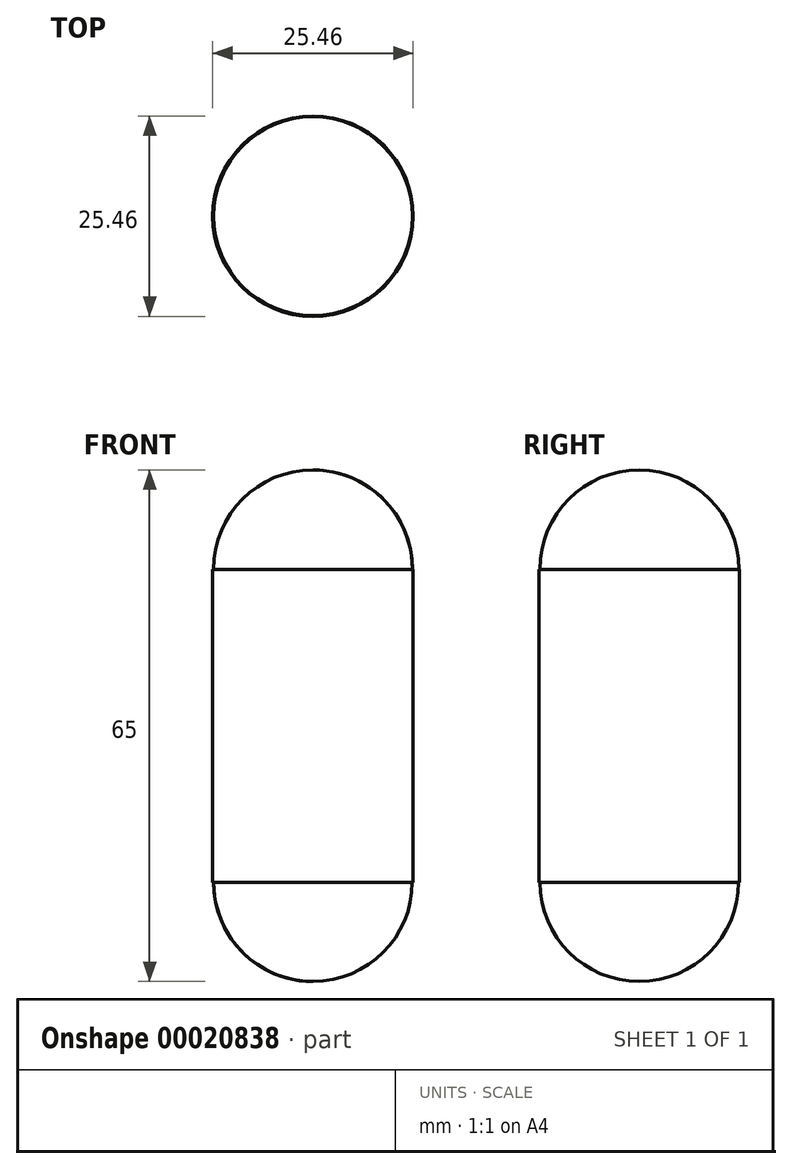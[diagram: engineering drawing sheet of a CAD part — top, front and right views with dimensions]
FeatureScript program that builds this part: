
annotation { "Feature Type Name" : "Feature", "Feature Type Description" : "" }
export const myFeature = defineFeature(function(context is Context, id is Id, definition is map)
    precondition{}
    {
        {
            var Q0;
            Q0=qCreatedBy(makeId("Front.planeOp"),FACE);
            var sketch = newSketch(context, id + "F0", { "sketchPlane" : qUnion([Q0])});
            skLineSegment(sketch, "E0.rect.bottom", {"start": v(-12.73, 19.88) * mm, "end": v(-12.63, 19.88) * mm});
            skLineSegment(sketch, "E0.rect.top", {"start": v(-12.73, -19.88) * mm, "end": v(0, -19.88) * mm});
            skLineSegment(sketch, "E0.rect.left", {"start": v(-12.73, 19.88) * mm, "end": v(-12.73, -19.88) * mm});
            skPoint(sketch, "E0.rect.middle", {"position": v(0, 0) * mm});
            skArc(sketch, "E1", {"start": v(0, 32.5) * mm, "mid": v(-12.63, 19.88) * mm, "end": v(0, 7.25) * mm});
            skArc(sketch, "E2", {"start": v(0, -7.27) * mm, "mid": v(-12.61, -19.88) * mm, "end": v(0, -32.5) * mm});
            skLineSegment(sketch, "E3", {"start": v(-12.73, 0) * mm, "end": v(0, 0) * mm});
            skLineSegment(sketch, "E4", {"start": v(0, 32.5) * mm, "end": v(0, -32.5) * mm});
            skLineSegment(sketch, "E5.trimOffspring", {"start": v(12.63, 19.88) * mm, "end": v(12.73, 19.88) * mm});
            skPoint(sketch, "E6.orphan", {"position": v(12.73, 0) * mm});
            skLineSegment(sketch, "E7.trimOffspring", {"start": v(12.61, -19.88) * mm, "end": v(12.73, -19.88) * mm});
            skSolve(sketch);
        }
        {
            var Q0;
            {var subQ4=sQuery(id+"F0.wireOp",EDGE,"E0.rect.bottom");Q0=makeQuery(id+"F0.imprint","IMPRINT",FACE,{"disambiguationData":[TD([[makeQuery(id+"F0.imprint","IMPRINT",EDGE,{"derivedFrom":subQ4}),-1.0]])]});}
            var Q1;
            {var subQ1=sQuery(id+"F0.wireOp",EDGE,"E1");var subQ4=makeQuery(id+"F0.imprint","INTERSECT",VERTEX,{"derivedFrom":[sQuery(id+"F0.wireOp",EDGE,"E0.rect.bottom"),subQ1]});Q1=makeQuery(id+"F0.imprint","IMPRINT",FACE,{"disambiguationData":[TD([[makeQuery(id+"F0.imprint","IMPRINT",EDGE,{"disambiguationData":[TD([[subQ4,1.0]])],"derivedFrom":subQ1}),1.0]])]});}
            var Q2;
            {var subQ1=sQuery(id+"F0.wireOp",EDGE,"E3");Q2=makeQuery(id+"F0.imprint","IMPRINT",FACE,{"disambiguationData":[TD([[makeQuery(id+"F0.imprint","IMPRINT",EDGE,{"derivedFrom":subQ1}),-1.0]])]});}
            var Q3;
            {var subQ0=sQuery(id+"F0.wireOp",EDGE,"E4");var subQ3=sQuery(id+"F0.wireOp",EDGE,"E0.rect.top");var subQ4=makeQuery(id+"F0.imprint","INTERSECT",VERTEX,{"derivedFrom":[subQ3,subQ0]});Q3=makeQuery(id+"F0.imprint","IMPRINT",FACE,{"disambiguationData":[TD([[makeQuery(id+"F0.imprint","IMPRINT",EDGE,{"disambiguationData":[TD([[subQ4,1.0]])],"derivedFrom":subQ3}),1.0]])]});}
            var Q4;
            {var subQ0=sQuery(id+"F0.wireOp",EDGE,"E4");var subQ3=sQuery(id+"F0.wireOp",EDGE,"E0.rect.top");var subQ4=makeQuery(id+"F0.imprint","INTERSECT",VERTEX,{"derivedFrom":[subQ3,subQ0]});Q4=makeQuery(id+"F0.imprint","IMPRINT",FACE,{"disambiguationData":[TD([[makeQuery(id+"F0.imprint","IMPRINT",EDGE,{"disambiguationData":[TD([[subQ4,1.0]])],"derivedFrom":subQ3}),-1.0]])]});}
            var Q5;
            Q5=sQuery(id+"F0.wireOp",EDGE,"E4");
            revolve(context, id + "F1", {"entities" : qUnion([Q0, Q1, Q2, Q3, Q4]), "axis" : qUnion([Q5]), "revolveType" : RevolveType.FULL});
        }
    });
